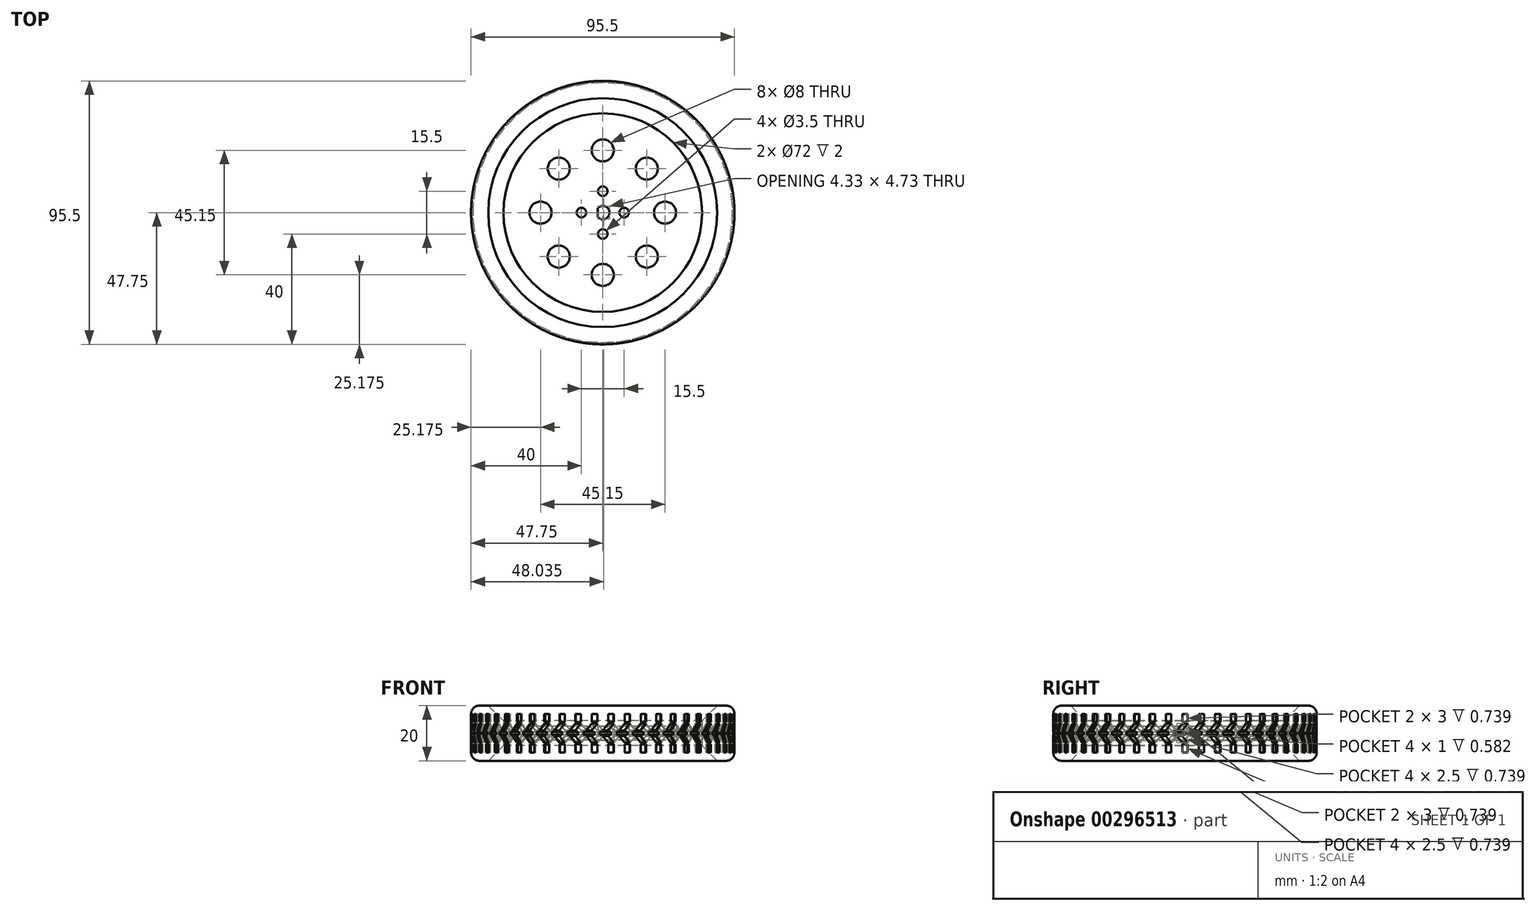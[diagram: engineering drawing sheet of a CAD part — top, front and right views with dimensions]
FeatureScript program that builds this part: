
annotation { "Feature Type Name" : "Feature", "Feature Type Description" : "" }
export const myFeature = defineFeature(function(context is Context, id is Id, definition is map)
    precondition{}
    {
        {
            assignVariable(context, id + "F0", {"name" : "TreadCount", "anyValue" : 50});
        }
        {
            var Q0;
            Q0=qCreatedBy(makeId("Top.planeOp"),FACE);
            var sketch = newSketch(context, id + "F1", { "sketchPlane" : qUnion([Q0])});
            skCircle(sketch, "E0", {"center": v(0, 0) * mm, "radius": 47.75 * mm});
            skCircle(sketch, "E1", {"center": v(0, 0) * mm, "radius": 44 * mm});
            skArc(sketch, "E2", {"start": v(-1.88, -1.57) * mm, "mid": v(2.45, 0) * mm, "end": v(-1.88, 1.57) * mm});
            skLineSegment(sketch, "E3", {"start": v(-1.88, -1.57) * mm, "end": v(-1.88, 1.57) * mm});
            skCircle(sketch, "E4", {"center": v(0, 0) * mm, "radius": 42.5 * mm});
            skCircle(sketch, "E5", {"center": v(0, 0) * mm, "radius": 36 * mm});
            skSolve(sketch);
        }
        {
            var Q0;
            Q0=makeQuery(id+"F1.imprint","IMPRINT",FACE,{"disambiguationData":[TD([[makeQuery(id+"F1.imprint","IMPRINT",EDGE,{"derivedFrom":sQuery(id+"F1.wireOp",EDGE,"E2")}),-1.0]])]});
            var Q1;
            Q1=makeQuery(id+"F1.imprint","IMPRINT",FACE,{"disambiguationData":[TD([[makeQuery(id+"F1.imprint","IMPRINT",EDGE,{"derivedFrom":sQuery(id+"F1.wireOp",EDGE,"8wvdLqEF-Mvgu-ieMB-92kP-JiN9EquYggHF")}),1.0]])]});
            extrude(context, id + "F2", {"entities" : qUnion([Q0, Q1]), "depth" : 12.5 * mm, "hasSecondDirection" : true, "secondDirectionOppositeDirection" : false, "secondDirectionDepth" : 7.5 * mm});
        }
        {
            var Q0;
            Q0=makeQuery(id+"F1.imprint","IMPRINT",FACE,{"disambiguationData":[TD([[makeQuery(id+"F1.imprint","IMPRINT",EDGE,{"derivedFrom":sQuery(id+"F1.wireOp",EDGE,"E4")}),1.0]])]});
            var Q1;
            Q1=makeQuery(id+"F1.imprint","IMPRINT",FACE,{"disambiguationData":[TD([[makeQuery(id+"F1.imprint","IMPRINT",EDGE,{"derivedFrom":sQuery(id+"F1.wireOp",EDGE,"E1")}),1.0]])]});
            extrude(context, id + "F3", {"entities" : qUnion([Q0, Q1]), "operationType" : NewBodyOperationType.ADD, "depth" : 20 * mm});
        }
        {
            var Q0;
            Q0=makeQuery(id+"F1.imprint","IMPRINT",FACE,{"disambiguationData":[TD([[makeQuery(id+"F1.imprint","IMPRINT",EDGE,{"derivedFrom":sQuery(id+"F1.wireOp",EDGE,"E0")}),1.0]])]});
            extrude(context, id + "F4", {"entities" : qUnion([Q0]), "depth" : 20 * mm});
        }
        {
            var Q0;
            Q0=makeQuery(id+"F1.imprint","IMPRINT",FACE,{"disambiguationData":[TD([[makeQuery(id+"F1.imprint","IMPRINT",EDGE,{"derivedFrom":sQuery(id+"F1.wireOp",EDGE,"E1")}),1.0]])]});
            extrude(context, id + "F5", {"entities" : qUnion([Q0]), "operationType" : NewBodyOperationType.REMOVE, "depth" : 1 * mm});
        }
        {
            var Q0;
            Q0=makeQuery(id+"F1.imprint","IMPRINT",FACE,{"disambiguationData":[TD([[makeQuery(id+"F1.imprint","IMPRINT",EDGE,{"derivedFrom":sQuery(id+"F1.wireOp",EDGE,"E1")}),1.0]])]});
            extrude(context, id + "F6", {"entities" : qUnion([Q0]), "operationType" : NewBodyOperationType.ADD, "depth" : 1 * mm});
        }
        {
            var Q0;
            Q0=makeQuery(id+"F1.imprint","IMPRINT",FACE,{"disambiguationData":[TD([[makeQuery(id+"F1.imprint","IMPRINT",EDGE,{"derivedFrom":sQuery(id+"F1.wireOp",EDGE,"E1")}),1.0]])]});
            extrude(context, id + "F7", {"entities" : qUnion([Q0]), "operationType" : NewBodyOperationType.REMOVE, "depth" : 20 * mm, "hasSecondDirection" : true, "secondDirectionOppositeDirection" : false, "secondDirectionDepth" : 19 * mm});
        }
        {
            var Q0;
            Q0=makeQuery(id+"F1.imprint","IMPRINT",FACE,{"disambiguationData":[TD([[makeQuery(id+"F1.imprint","IMPRINT",EDGE,{"derivedFrom":sQuery(id+"F1.wireOp",EDGE,"E1")}),1.0]])]});
            extrude(context, id + "F8", {"entities" : qUnion([Q0]), "operationType" : NewBodyOperationType.ADD, "depth" : 20 * mm, "hasSecondDirection" : true, "secondDirectionOppositeDirection" : false, "secondDirectionDepth" : 19 * mm});
        }
        {
            var Q0;
            Q0=makeQuery(id+"F2.opExtrude","CAP_FACE",FACE,{"disambiguationData":[OSD([sQuery(id+"F1.wireOp",EDGE,"E2"),sQuery(id+"F1.wireOp",EDGE,"E3"),sQuery(id+"F1.wireOp",EDGE,"E5")])],"isStart":false});
            var sketch = newSketch(context, id + "F9", { "sketchPlane" : qUnion([Q0])});
            skCircle(sketch, "E6", {"center": v(0, 0) * mm, "radius": 12.5 * mm});
            skSolve(sketch);
        }
        {
            var Q0;
            {var subQ0=sQuery(id+"F1.wireOp",EDGE,"E2");Q0=makeQuery(id+"F9.imprint","IMPRINT",FACE,{"disambiguationData":[TD([[makeQuery(id+"F9.imprint","IMPRINT",EDGE,{"derivedFrom":makeQuery(id+"F2.opExtrude","CAP_EDGE",EDGE,{"disambiguationData":[OSD([subQ0])],"isStart":false})}),-1.0]])]});}
            var sketch = newSketch(context, id + "F10", { "sketchPlane" : qUnion([Q0])});
            skCircle(sketch, "E7", {"center": v(0, 22.58) * mm, "radius": 4 * mm});
            skCircle(sketch, "E8", {"center": v(0, 0) * mm, "radius": 5 * mm});
            skSolve(sketch);
        }
        {
            var Q0;
            Q0=makeQuery(id+"F10.imprint","IMPRINT",FACE,{"disambiguationData":[TD([[makeQuery(id+"F10.imprint","IMPRINT",EDGE,{"derivedFrom":sQuery(id+"F10.wireOp",EDGE,"E7")}),1.0]])]});
            extrude(context, id + "F11", {"entities" : qUnion([Q0]), "depth" : 25 * mm, "hasSecondDirection" : true, "secondDirectionOppositeDirection" : true, "secondDirectionDepth" : 25 * mm});
        }
        {
            var Q0;
            Q0=makeQuery(id+"F11.opExtrude","SWEPT_BODY",BODY,{"disambiguationData":[OSD([sQuery(id+"F10.wireOp",EDGE,"E7")])]});
            var Q1;
            Q1=sQuery(id+"F10.wireOp",EDGE,"E8");
            circularPattern(context, id + "F12", {"operationType" : NewBodyOperationType.REMOVE, "entities" : qUnion([Q0]), "axis" : qUnion([Q1]), "angle" : 360 * degree, "instanceCount" : 8, "equalSpace" : true});
        }
        {
            var Q0;
            Q0=makeQuery(id+"F3.opExtrude","CAP_EDGE",EDGE,{"disambiguationData":[OSD([sQuery(id+"F1.wireOp",EDGE,"E5")])],"isStart":false});
            var Q1;
            Q1=makeQuery(id+"F3.opExtrude","CAP_EDGE",EDGE,{"disambiguationData":[OSD([sQuery(id+"F1.wireOp",EDGE,"E5")])],"isStart":true});
            chamfer(context, id + "F13", {"entities" : qUnion([Q0, Q1]), "width" : 5.5 * mm, "tangentPropagation" : true});
        }
        {
            var Q0;
            Q0=makeQuery(id+"F12.boolean.opBoolean","INTERSECT",EDGE,{"derivedFrom":[makeQuery(id+"F2.opExtrude","CAP_FACE",FACE,{"disambiguationData":[OSD([sQuery(id+"F1.wireOp",EDGE,"E2"),sQuery(id+"F1.wireOp",EDGE,"E3"),sQuery(id+"F1.wireOp",EDGE,"E5")])],"isStart":false}),makeQuery(id+"F12.opPattern","COPY",FACE,{"derivedFrom":makeQuery(id+"F11.opExtrude","SWEPT_FACE",FACE,{"disambiguationData":[OSD([sQuery(id+"F10.wireOp",EDGE,"E7")])]}),"instanceName":"3"})]});
            var Q1;
            Q1=makeQuery(id+"F12.boolean.opBoolean","INTERSECT",EDGE,{"derivedFrom":[makeQuery(id+"F2.opExtrude","CAP_FACE",FACE,{"disambiguationData":[OSD([sQuery(id+"F1.wireOp",EDGE,"E2"),sQuery(id+"F1.wireOp",EDGE,"E3"),sQuery(id+"F1.wireOp",EDGE,"E5")])],"isStart":false}),makeQuery(id+"F12.opPattern","COPY",FACE,{"derivedFrom":makeQuery(id+"F11.opExtrude","SWEPT_FACE",FACE,{"disambiguationData":[OSD([sQuery(id+"F10.wireOp",EDGE,"E7")])]}),"instanceName":"4"})]});
            var Q2;
            Q2=makeQuery(id+"F12.boolean.opBoolean","INTERSECT",EDGE,{"derivedFrom":[makeQuery(id+"F2.opExtrude","CAP_FACE",FACE,{"disambiguationData":[OSD([sQuery(id+"F1.wireOp",EDGE,"E2"),sQuery(id+"F1.wireOp",EDGE,"E3"),sQuery(id+"F1.wireOp",EDGE,"E5")])],"isStart":false}),makeQuery(id+"F12.opPattern","COPY",FACE,{"derivedFrom":makeQuery(id+"F11.opExtrude","SWEPT_FACE",FACE,{"disambiguationData":[OSD([sQuery(id+"F10.wireOp",EDGE,"E7")])]}),"instanceName":"2"})]});
            var Q3;
            Q3=makeQuery(id+"F12.boolean.opBoolean","INTERSECT",EDGE,{"derivedFrom":[makeQuery(id+"F2.opExtrude","CAP_FACE",FACE,{"disambiguationData":[OSD([sQuery(id+"F1.wireOp",EDGE,"E2"),sQuery(id+"F1.wireOp",EDGE,"E3"),sQuery(id+"F1.wireOp",EDGE,"E5")])],"isStart":false}),makeQuery(id+"F12.opPattern","COPY",FACE,{"derivedFrom":makeQuery(id+"F11.opExtrude","SWEPT_FACE",FACE,{"disambiguationData":[OSD([sQuery(id+"F10.wireOp",EDGE,"E7")])]}),"instanceName":"1"})]});
            var Q4;
            Q4=makeQuery(id+"F12.boolean.opBoolean","INTERSECT",EDGE,{"derivedFrom":[makeQuery(id+"F2.opExtrude","CAP_FACE",FACE,{"disambiguationData":[OSD([sQuery(id+"F1.wireOp",EDGE,"E2"),sQuery(id+"F1.wireOp",EDGE,"E3"),sQuery(id+"F1.wireOp",EDGE,"E5")])],"isStart":false}),makeQuery(id+"F11.opExtrude","SWEPT_FACE",FACE,{"disambiguationData":[OSD([sQuery(id+"F10.wireOp",EDGE,"E7")])]})]});
            var Q5;
            Q5=makeQuery(id+"F12.boolean.opBoolean","INTERSECT",EDGE,{"derivedFrom":[makeQuery(id+"F2.opExtrude","CAP_FACE",FACE,{"disambiguationData":[OSD([sQuery(id+"F1.wireOp",EDGE,"E2"),sQuery(id+"F1.wireOp",EDGE,"E3"),sQuery(id+"F1.wireOp",EDGE,"E5")])],"isStart":false}),makeQuery(id+"F12.opPattern","COPY",FACE,{"derivedFrom":makeQuery(id+"F11.opExtrude","SWEPT_FACE",FACE,{"disambiguationData":[OSD([sQuery(id+"F10.wireOp",EDGE,"E7")])]}),"instanceName":"7"})]});
            var Q6;
            Q6=makeQuery(id+"F12.boolean.opBoolean","INTERSECT",EDGE,{"derivedFrom":[makeQuery(id+"F2.opExtrude","CAP_FACE",FACE,{"disambiguationData":[OSD([sQuery(id+"F1.wireOp",EDGE,"E2"),sQuery(id+"F1.wireOp",EDGE,"E3"),sQuery(id+"F1.wireOp",EDGE,"E5")])],"isStart":false}),makeQuery(id+"F12.opPattern","COPY",FACE,{"derivedFrom":makeQuery(id+"F11.opExtrude","SWEPT_FACE",FACE,{"disambiguationData":[OSD([sQuery(id+"F10.wireOp",EDGE,"E7")])]}),"instanceName":"6"})]});
            var Q7;
            Q7=makeQuery(id+"F12.boolean.opBoolean","INTERSECT",EDGE,{"derivedFrom":[makeQuery(id+"F2.opExtrude","CAP_FACE",FACE,{"disambiguationData":[OSD([sQuery(id+"F1.wireOp",EDGE,"E2"),sQuery(id+"F1.wireOp",EDGE,"E3"),sQuery(id+"F1.wireOp",EDGE,"E5")])],"isStart":false}),makeQuery(id+"F12.opPattern","COPY",FACE,{"derivedFrom":makeQuery(id+"F11.opExtrude","SWEPT_FACE",FACE,{"disambiguationData":[OSD([sQuery(id+"F10.wireOp",EDGE,"E7")])]}),"instanceName":"5"})]});
            var Q8;
            {var subQ0=sQuery(id+"F9.wireOp",EDGE,"E6");Q8=makeQuery(id+"FrM5SCEm5QlvkcH_3.opChamfer","BLEND_EDGE",EDGE,{"blendedFrom":[makeQuery(id+"Ft7B6tNihZhRfeO_3.opExtrude","CAP_EDGE",EDGE,{"disambiguationData":[OSD([subQ0])],"isStart":false}),makeQuery(id+"Ft7B6tNihZhRfeO_3.opExtrude","CAP_FACE",FACE,{"disambiguationData":[OSD([sQuery(id+"F1.wireOp",EDGE,"E2"),sQuery(id+"F1.wireOp",EDGE,"E3"),subQ0])],"isStart":false})],"blendedInto":[makeQuery(id+"Ft7B6tNihZhRfeO_3.opExtrude","CAP_FACE",FACE,{"disambiguationData":[OSD([sQuery(id+"F1.wireOp",EDGE,"E2"),sQuery(id+"F1.wireOp",EDGE,"E3"),subQ0])],"isStart":false})]});}
            var Q9;
            Q9=makeQuery(id+"F12.boolean.opBoolean","INTERSECT",EDGE,{"derivedFrom":[makeQuery(id+"F2.opExtrude","CAP_FACE",FACE,{"disambiguationData":[OSD([sQuery(id+"F1.wireOp",EDGE,"E2"),sQuery(id+"F1.wireOp",EDGE,"E3"),sQuery(id+"F1.wireOp",EDGE,"E5")])],"isStart":true}),makeQuery(id+"F12.opPattern","COPY",FACE,{"derivedFrom":makeQuery(id+"F11.opExtrude","SWEPT_FACE",FACE,{"disambiguationData":[OSD([sQuery(id+"F10.wireOp",EDGE,"E7")])]}),"instanceName":"6"})]});
            var Q10;
            Q10=makeQuery(id+"F12.boolean.opBoolean","INTERSECT",EDGE,{"derivedFrom":[makeQuery(id+"F2.opExtrude","CAP_FACE",FACE,{"disambiguationData":[OSD([sQuery(id+"F1.wireOp",EDGE,"E2"),sQuery(id+"F1.wireOp",EDGE,"E3"),sQuery(id+"F1.wireOp",EDGE,"E5")])],"isStart":true}),makeQuery(id+"F12.opPattern","COPY",FACE,{"derivedFrom":makeQuery(id+"F11.opExtrude","SWEPT_FACE",FACE,{"disambiguationData":[OSD([sQuery(id+"F10.wireOp",EDGE,"E7")])]}),"instanceName":"5"})]});
            var Q11;
            Q11=makeQuery(id+"F12.boolean.opBoolean","INTERSECT",EDGE,{"derivedFrom":[makeQuery(id+"F2.opExtrude","CAP_FACE",FACE,{"disambiguationData":[OSD([sQuery(id+"F1.wireOp",EDGE,"E2"),sQuery(id+"F1.wireOp",EDGE,"E3"),sQuery(id+"F1.wireOp",EDGE,"E5")])],"isStart":true}),makeQuery(id+"F12.opPattern","COPY",FACE,{"derivedFrom":makeQuery(id+"F11.opExtrude","SWEPT_FACE",FACE,{"disambiguationData":[OSD([sQuery(id+"F10.wireOp",EDGE,"E7")])]}),"instanceName":"4"})]});
            var Q12;
            Q12=makeQuery(id+"F12.boolean.opBoolean","INTERSECT",EDGE,{"derivedFrom":[makeQuery(id+"F2.opExtrude","CAP_FACE",FACE,{"disambiguationData":[OSD([sQuery(id+"F1.wireOp",EDGE,"E2"),sQuery(id+"F1.wireOp",EDGE,"E3"),sQuery(id+"F1.wireOp",EDGE,"E5")])],"isStart":true}),makeQuery(id+"F12.opPattern","COPY",FACE,{"derivedFrom":makeQuery(id+"F11.opExtrude","SWEPT_FACE",FACE,{"disambiguationData":[OSD([sQuery(id+"F10.wireOp",EDGE,"E7")])]}),"instanceName":"3"})]});
            var Q13;
            Q13=makeQuery(id+"F12.boolean.opBoolean","INTERSECT",EDGE,{"derivedFrom":[makeQuery(id+"F2.opExtrude","CAP_FACE",FACE,{"disambiguationData":[OSD([sQuery(id+"F1.wireOp",EDGE,"E2"),sQuery(id+"F1.wireOp",EDGE,"E3"),sQuery(id+"F1.wireOp",EDGE,"E5")])],"isStart":true}),makeQuery(id+"F12.opPattern","COPY",FACE,{"derivedFrom":makeQuery(id+"F11.opExtrude","SWEPT_FACE",FACE,{"disambiguationData":[OSD([sQuery(id+"F10.wireOp",EDGE,"E7")])]}),"instanceName":"2"})]});
            var Q14;
            Q14=makeQuery(id+"F12.boolean.opBoolean","INTERSECT",EDGE,{"derivedFrom":[makeQuery(id+"F2.opExtrude","CAP_FACE",FACE,{"disambiguationData":[OSD([sQuery(id+"F1.wireOp",EDGE,"E2"),sQuery(id+"F1.wireOp",EDGE,"E3"),sQuery(id+"F1.wireOp",EDGE,"E5")])],"isStart":true}),makeQuery(id+"F12.opPattern","COPY",FACE,{"derivedFrom":makeQuery(id+"F11.opExtrude","SWEPT_FACE",FACE,{"disambiguationData":[OSD([sQuery(id+"F10.wireOp",EDGE,"E7")])]}),"instanceName":"1"})]});
            var Q15;
            Q15=makeQuery(id+"F12.boolean.opBoolean","INTERSECT",EDGE,{"derivedFrom":[makeQuery(id+"F2.opExtrude","CAP_FACE",FACE,{"disambiguationData":[OSD([sQuery(id+"F1.wireOp",EDGE,"E2"),sQuery(id+"F1.wireOp",EDGE,"E3"),sQuery(id+"F1.wireOp",EDGE,"E5")])],"isStart":true}),makeQuery(id+"F11.opExtrude","SWEPT_FACE",FACE,{"disambiguationData":[OSD([sQuery(id+"F10.wireOp",EDGE,"E7")])]})]});
            var Q16;
            {var subQ0=sQuery(id+"F9.wireOp",EDGE,"E6");Q16=makeQuery(id+"FrM5SCEm5QlvkcH_3.opChamfer","BLEND_EDGE",EDGE,{"blendedFrom":[makeQuery(id+"Ft7B6tNihZhRfeO_3.opExtrude","CAP_EDGE",EDGE,{"disambiguationData":[OSD([subQ0])],"isStart":true}),makeQuery(id+"Ft7B6tNihZhRfeO_3.opExtrude","CAP_FACE",FACE,{"disambiguationData":[OSD([sQuery(id+"F1.wireOp",EDGE,"E2"),sQuery(id+"F1.wireOp",EDGE,"E3"),subQ0])],"isStart":true})],"blendedInto":[makeQuery(id+"Ft7B6tNihZhRfeO_3.opExtrude","CAP_FACE",FACE,{"disambiguationData":[OSD([sQuery(id+"F1.wireOp",EDGE,"E2"),sQuery(id+"F1.wireOp",EDGE,"E3"),subQ0])],"isStart":true})]});}
            var Q17;
            Q17=makeQuery(id+"F12.boolean.opBoolean","INTERSECT",EDGE,{"derivedFrom":[makeQuery(id+"F2.opExtrude","CAP_FACE",FACE,{"disambiguationData":[OSD([sQuery(id+"F1.wireOp",EDGE,"E2"),sQuery(id+"F1.wireOp",EDGE,"E3"),sQuery(id+"F1.wireOp",EDGE,"E5")])],"isStart":true}),makeQuery(id+"F12.opPattern","COPY",FACE,{"derivedFrom":makeQuery(id+"F11.opExtrude","SWEPT_FACE",FACE,{"disambiguationData":[OSD([sQuery(id+"F10.wireOp",EDGE,"E7")])]}),"instanceName":"7"})]});
            fillet(context, id + "F14", {"entities" : qUnion([Q0, Q1, Q2, Q3, Q4, Q5, Q6, Q7, Q8, Q9, Q10, Q11, Q12, Q13, Q14, Q15, Q16, Q17]), "radius" : 1 * mm, "tangentPropagation" : true, "allowEdgeOverflow" : false});
        }
        {
            var Q0;
            Q0=qCreatedBy(makeId("Right.planeOp"),FACE);
            cPlane(context, id + "F15", {"entities" : qUnion([Q0]), "cplaneType" : CPlaneType.OFFSET, "offset" : 48 * mm, "width" : 150 * mm, "height" : 150 * mm});
        }
        {
            var Q0;
            Q0=qCreatedBy(id+"F15.planeOp",FACE);
            var sketch = newSketch(context, id + "F16", { "sketchPlane" : qUnion([Q0])});
            skPoint(sketch, "E9", {"position": v(0, 10) * mm});
            skLineSegment(sketch, "E10.bottom", {"start": v(-1, 17) * mm, "end": v(1, 17) * mm});
            skLineSegment(sketch, "E10.top", {"start": v(-1, 14) * mm, "end": v(1, 14) * mm});
            skLineSegment(sketch, "E10.left", {"start": v(-1, 17) * mm, "end": v(-1, 14) * mm});
            skLineSegment(sketch, "E10.right", {"start": v(1, 17) * mm, "end": v(1, 14) * mm});
            skLineSegment(sketch, "E11", {"start": v(0, 10) * mm, "end": v(-8.56, 10) * mm});
            skLineSegment(sketch, "E12.MirrorCS", {"start": v(-1, 6) * mm, "end": v(1, 6) * mm});
            skLineSegment(sketch, "E13.MirrorCS", {"start": v(-1, 3) * mm, "end": v(-1, 6) * mm});
            skLineSegment(sketch, "E14.MirrorCS", {"start": v(1, 3) * mm, "end": v(1, 6) * mm});
            skLineSegment(sketch, "E15.MirrorCS", {"start": v(-1, 3) * mm, "end": v(1, 3) * mm});
            skLineSegment(sketch, "E16.bottom", {"start": v(-1, 13.5) * mm, "end": v(1, 13.5) * mm});
            skPoint(sketch, "E17", {"position": v(-3, 11) * mm});
            skLineSegment(sketch, "E18", {"start": v(-3, 11) * mm, "end": v(-1, 13.5) * mm});
            skLineSegment(sketch, "E19.MirrorCS", {"start": v(-3, 9) * mm, "end": v(-1, 6.5) * mm});
            skLineSegment(sketch, "E20.MirrorCS", {"start": v(-1, 6.5) * mm, "end": v(1, 6.5) * mm});
            skPoint(sketch, "E21", {"position": v(-1, 11) * mm});
            skLineSegment(sketch, "E22", {"start": v(-3, 11) * mm, "end": v(-1, 11) * mm});
            skLineSegment(sketch, "E23", {"start": v(-1, 11) * mm, "end": v(1, 13.5) * mm});
            skLineSegment(sketch, "E24.MirrorCS", {"start": v(-3, 9) * mm, "end": v(-1, 9) * mm});
            skLineSegment(sketch, "E25.MirrorCS", {"start": v(-1, 9) * mm, "end": v(1, 6.5) * mm});
            skLineSegment(sketch, "E26.bottom", {"start": v(-4, 10.5) * mm, "end": v(0, 10.5) * mm});
            skLineSegment(sketch, "E26.top", {"start": v(-4, 9.5) * mm, "end": v(0, 9.5) * mm});
            skLineSegment(sketch, "E26.left", {"start": v(-4, 10.5) * mm, "end": v(-4, 9.5) * mm});
            skLineSegment(sketch, "E26.right", {"start": v(0, 10.5) * mm, "end": v(0, 9.5) * mm});
            skPoint(sketch, "E26.middle", {"position": v(-2, 10) * mm});
            skSolve(sketch);
        }
        {
            var Q0;
            Q0=makeQuery(id+"F16.imprint","IMPRINT",FACE,{"disambiguationData":[TD([[makeQuery(id+"F16.imprint","IMPRINT",EDGE,{"derivedFrom":sQuery(id+"F16.wireOp",EDGE,"E10.bottom")}),-1.0]])]});
            var Q1;
            Q1=makeQuery(id+"F16.imprint","IMPRINT",FACE,{"disambiguationData":[TD([[makeQuery(id+"F16.imprint","IMPRINT",EDGE,{"derivedFrom":sQuery(id+"F16.wireOp",EDGE,"E16.bottom")}),-1.0]])]});
            var Q2;
            Q2=makeQuery(id+"F16.imprint","IMPRINT",FACE,{"disambiguationData":[TD([[makeQuery(id+"F16.imprint","IMPRINT",EDGE,{"derivedFrom":sQuery(id+"F16.wireOp",EDGE,"c6fea6ce-3147-4b6b-9fa2-a9a93d3b0bdf0.MirrorCS")}),-1.0]])]});
            var Q3;
            Q3=makeQuery(id+"F16.imprint","IMPRINT",FACE,{"disambiguationData":[TD([[makeQuery(id+"F16.imprint","IMPRINT",EDGE,{"derivedFrom":sQuery(id+"F16.wireOp",EDGE,"E12.MirrorCS")}),-1.0]])]});
            var Q4;
            Q4=makeQuery(id+"F16.imprint","IMPRINT",FACE,{"disambiguationData":[TD([[makeQuery(id+"F16.imprint","IMPRINT",EDGE,{"derivedFrom":sQuery(id+"F16.wireOp",EDGE,"E19.MirrorCS")}),1.0]])]});
            var Q5;
            {var subQ5=sQuery(id+"F16.wireOp",EDGE,"E26.top");Q5=makeQuery(id+"F16.imprint","IMPRINT",FACE,{"disambiguationData":[TD([[makeQuery(id+"F16.imprint","IMPRINT",EDGE,{"derivedFrom":subQ5}),1.0]])]});}
            var Q6;
            {var subQ5=sQuery(id+"F16.wireOp",EDGE,"E26.bottom");Q6=makeQuery(id+"F16.imprint","IMPRINT",FACE,{"disambiguationData":[TD([[makeQuery(id+"F16.imprint","IMPRINT",EDGE,{"derivedFrom":subQ5}),-1.0]])]});}
            extrude(context, id + "F17", {"entities" : qUnion([Q0, Q1, Q2, Q3, Q4, Q5, Q6]), "oppositeDirection" : true, "depth" : 1 * mm, "hasSecondDirection" : true, "secondDirectionOppositeDirection" : false, "secondDirectionDepth" : 5 * mm});
        }
        {
            var Q0;
            Q0=makeQuery(id+"F17.opExtrude","SWEPT_BODY",BODY,{"disambiguationData":[OSD([sQuery(id+"F16.wireOp",EDGE,"E26.bottom"),sQuery(id+"F16.wireOp",EDGE,"E26.top"),sQuery(id+"F16.wireOp",EDGE,"E26.left"),sQuery(id+"F16.wireOp",EDGE,"E26.right")])]});
            var Q1;
            Q1=makeQuery(id+"F17.opExtrude","SWEPT_BODY",BODY,{"disambiguationData":[OSD([sQuery(id+"F16.wireOp",EDGE,"E16.bottom"),sQuery(id+"F16.wireOp",EDGE,"E18"),sQuery(id+"F16.wireOp",EDGE,"E22"),sQuery(id+"F16.wireOp",EDGE,"E23")])]});
            var Q2;
            Q2=makeQuery(id+"F17.opExtrude","SWEPT_BODY",BODY,{"disambiguationData":[OSD([sQuery(id+"F16.wireOp",EDGE,"E10.bottom"),sQuery(id+"F16.wireOp",EDGE,"E10.top"),sQuery(id+"F16.wireOp",EDGE,"E10.left"),sQuery(id+"F16.wireOp",EDGE,"E10.right")])]});
            var Q3;
            Q3=makeQuery(id+"F17.opExtrude","SWEPT_BODY",BODY,{"disambiguationData":[OSD([sQuery(id+"F16.wireOp",EDGE,"E19.MirrorCS"),sQuery(id+"F16.wireOp",EDGE,"E20.MirrorCS"),sQuery(id+"F16.wireOp",EDGE,"E24.MirrorCS"),sQuery(id+"F16.wireOp",EDGE,"E25.MirrorCS")])]});
            var Q4;
            Q4=makeQuery(id+"F17.opExtrude","SWEPT_BODY",BODY,{"disambiguationData":[OSD([sQuery(id+"F16.wireOp",EDGE,"E12.MirrorCS"),sQuery(id+"F16.wireOp",EDGE,"E13.MirrorCS"),sQuery(id+"F16.wireOp",EDGE,"E14.MirrorCS"),sQuery(id+"F16.wireOp",EDGE,"E15.MirrorCS")])]});
            var Q5;
            {var subQ0=sQuery(id+"F1.wireOp",EDGE,"E5");Q5=makeQuery(id+"F13.opChamfer","BLEND_EDGE",EDGE,{"blendedFrom":[makeQuery(id+"F3.opExtrude","CAP_EDGE",EDGE,{"disambiguationData":[OSD([subQ0])],"isStart":false}),makeQuery(id+"F3.opExtrude","CAP_FACE",FACE,{"disambiguationData":[OSD([sQuery(id+"F1.wireOp",EDGE,"E1"),subQ0])],"isStart":false})],"blendedInto":[makeQuery(id+"F3.opExtrude","CAP_FACE",FACE,{"disambiguationData":[OSD([sQuery(id+"F1.wireOp",EDGE,"E1"),subQ0])],"isStart":false})]});}
            circularPattern(context, id + "F18", {"operationType" : NewBodyOperationType.REMOVE, "entities" : qUnion([Q0, Q1, Q2, Q3, Q4]), "axis" : qUnion([Q5]), "angle" : 360 * degree, "instanceCount" : getVariable(context, 'TreadCount'), "equalSpace" : true});
        }
        {
            var Q0;
            Q0=makeQuery(id+"F4.opExtrude","CAP_EDGE",EDGE,{"disambiguationData":[OSD([sQuery(id+"F1.wireOp",EDGE,"E0")])],"isStart":false});
            var Q1;
            Q1=makeQuery(id+"F4.opExtrude","CAP_EDGE",EDGE,{"disambiguationData":[OSD([sQuery(id+"F1.wireOp",EDGE,"E0")])],"isStart":true});
            fillet(context, id + "F19", {"entities" : qUnion([Q0, Q1]), "radius" : 3 * mm, "tangentPropagation" : true, "allowEdgeOverflow" : false});
        }
        {
            var Q0;
            Q0=makeQuery(id+"F9.imprint","IMPRINT",FACE,{"disambiguationData":[TD([[makeQuery(id+"F9.imprint","IMPRINT",EDGE,{"derivedFrom":sQuery(id+"F9.wireOp",EDGE,"E6")}),1.0]])]});
            var sketch = newSketch(context, id + "F20", { "sketchPlane" : qUnion([Q0])});
            skCircle(sketch, "E27", {"center": v(0, 0) * mm, "radius": 11.25 * mm});
            skCircle(sketch, "E28", {"center": v(0, 7.75) * mm, "radius": 1.75 * mm});
            skCircle(sketch, "E29", {"center": v(0, 0) * mm, "radius": 2.5 * mm});
            skSolve(sketch);
        }
        {
            var Q0;
            Q0=makeQuery(id+"F20.imprint","IMPRINT",FACE,{"disambiguationData":[TD([[makeQuery(id+"F20.imprint","IMPRINT",EDGE,{"derivedFrom":sQuery(id+"F20.wireOp",EDGE,"E28")}),1.0]])]});
            extrude(context, id + "F21", {"entities" : qUnion([Q0]), "depth" : 25 * mm, "hasSecondDirection" : true, "secondDirectionOppositeDirection" : true, "secondDirectionDepth" : 25 * mm});
        }
        {
            var Q0;
            Q0=makeQuery(id+"F21.opExtrude","SWEPT_BODY",BODY,{"disambiguationData":[OSD([sQuery(id+"F20.wireOp",EDGE,"E28")])]});
            var Q1;
            Q1=sQuery(id+"F9.wireOp",EDGE,"E6");
            circularPattern(context, id + "F22", {"operationType" : NewBodyOperationType.REMOVE, "entities" : qUnion([Q0]), "axis" : qUnion([Q1]), "angle" : 360 * degree, "instanceCount" : 4, "equalSpace" : true});
        }
    });
